# Revit family: FU_Stool_Sandler_YUMI 4-1
name_source: partatom
category: Furniture
units: mm (PartAtom-declared; Revit-internal decimal feet)

## family parameters
Always vertical = No
Cut with Voids When Loaded = No
OmniClass Number = 23.21.23.15.17
Render Appearance Source = Family Geometry
Room Calculation Point = No
Shared = No
Work Plane-Based = Yes

## types (1)
- YUMI 4.1
    BIMobject category = Chair
    BIMobject category code = furniture-chair
    BIMobject main category = Furniture
    BIMobject main category code = furniture
    Brand url = https://www.sandlerseating.com
    Default Elevation = 1219.2 mm  [stored 4 ft]
    Description = Chair
    Design country = UK
    Edition number = 1
    Frame = BS03 - YUMI
    Frame Material = Wood - Walnut Beech
    IFC Classification = Furnishing Element
    MAX HEIGHT = 987 mm  [stored 3.23819 ft]
    MIN HEIGHT = 848 mm  [stored 2.78215 ft]
    Manufacturer = Sandler
    Manufacturer country = UK
    Manufacturer name = Sandler
    Masterformat 2014 Code = 12 48 43.13
    Masterformat 2014 Description = Chair Mats
    Model = YUMI 4.1
    OmniClass Code = 23-21 23 15 17
    Product Guid = ??
    Product data url = https://www.sandlerseating.com
    Product family = Furniture
    Product group = Chair
    Product name = YUMI 4.1
    Requested Height = 987 mm  [stored 3.23819 ft]
    Seat = TP01 - YUMI
    Seat Material = Fabric - Manhattan - Lexington YI113
    Uniformat II Description = Movable Furnishings
    depth = 520 mm  [stored 1.70604 ft]
    height = 987 mm  [stored 3.23819 ft]
    width = 465 mm  [stored 1.52559 ft]

note: [stored X ft] marks values corroborated as IEEE doubles in the binary element streams (Revit-internal decimal feet)

## geometry (parser evidence)
native form markers: Sweep x7
no freeform markers — native parametric forms only
